# Revit family: NLRS_33_GM_FB_TC_STORAX_vloerluikladder_DLL-IH3
name_source: partatom
category: Generic Models
revit_build: Autodesk Revit 2015 (Build: 20140223_1515(x64)
units: mm (PartAtom-declared; Revit-internal decimal feet)

## types (6) — shared parameters
Manufacturer = Storax
Model = DLL-IH
URL = http://www.storax.nl
antislip profilering = Yes
belasting totaal = 150.00 kg
breedte ladderdeel 1 = 500 mm  [stored 1.64042 ft]
breedte ladderdeel 2 = 430 mm
breedte ladderdeel 3 = 360 mm  [stored 1.1811 ft]
code productgroep = LUI
conservering = brut
false = No
garantietermijn in jaren = 5
inhaakbeugel en weghangbakje = Yes
materiaal = bcb_aluminium
modeler = Bouwconnect
normering = NEN 2484/EN 131
omschrijving = dakluikladder
productgroep = Dakluiken
slotbeugel = Yes
true = Yes
uitschuifbare leuning = Yes
zero-valued in all types: Default Elevation

## per-type parameters (varying)
| type | aantal sporten | hoogte | lengte ladderdeel |
| DLL-IH3/345 | 7 | 3450 mm  [stored 11.3189 ft] | 1900 mm  [stored 6.2336 ft] |
| DLL-IH3/430 | 8 | 4300 mm | 2150 mm |
| DLL-IH3/495 | 9 | 4950 mm | 2650 mm |
| DLL-IH3/565 | 10 | 5650 mm | 3150 mm |
| DLL-IH3/690 | 12 | 6900 mm | 3150 mm |
| DLL-IH3/800 | 14 | 8000 mm | 3650 mm |

note: [stored X ft] marks values corroborated as IEEE doubles in the binary element streams (Revit-internal decimal feet)

## geometry (parser evidence)
native form markers: Blend x4, Sweep x11
no freeform markers — native parametric forms only
